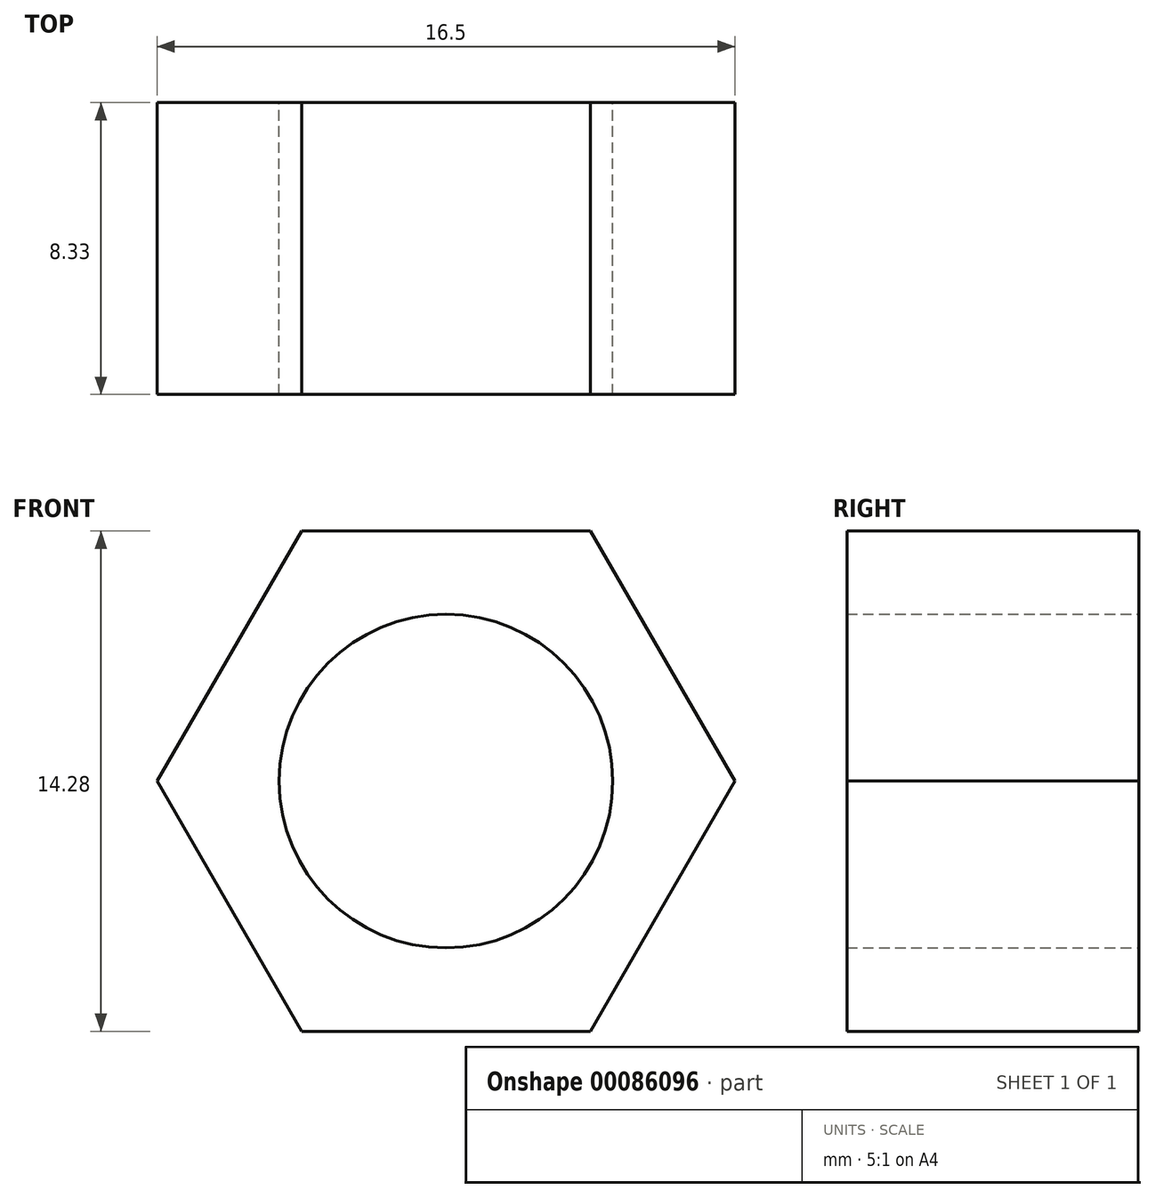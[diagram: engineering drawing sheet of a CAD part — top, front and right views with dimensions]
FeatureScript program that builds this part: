
annotation { "Feature Type Name" : "Feature", "Feature Type Description" : "" }
export const myFeature = defineFeature(function(context is Context, id is Id, definition is map)
    precondition{}
    {
        {
            var Q0;
            Q0=qCreatedBy(makeId("Front.planeOp"),FACE);
            var sketch = newSketch(context, id + "F0", { "sketchPlane" : qUnion([Q0])});
            skCircle(sketch, "E0.cCircle", {"center": v(0, 0) * mm, "radius": 7.14 * mm, "construction": true});
            skLineSegment(sketch, "E0.0", {"start": v(4.12, -7.14) * mm, "end": v(-4.12, -7.14) * mm});
            skLineSegment(sketch, "E0.1", {"start": v(-4.12, -7.14) * mm, "end": v(-8.25, 0) * mm});
            skLineSegment(sketch, "E0.2", {"start": v(-8.25, 0) * mm, "end": v(-4.12, 7.14) * mm});
            skLineSegment(sketch, "E0.3", {"start": v(-4.12, 7.14) * mm, "end": v(4.12, 7.14) * mm});
            skLineSegment(sketch, "E0.4", {"start": v(4.12, 7.14) * mm, "end": v(8.25, 0) * mm});
            skLineSegment(sketch, "E0.5", {"start": v(8.25, 0) * mm, "end": v(4.12, -7.14) * mm});
            skPoint(sketch, "E0.0.midPoint", {"position": v(0, -7.14) * mm});
            skCircle(sketch, "E1", {"center": v(0, 0) * mm, "radius": 4.76 * mm});
            skSolve(sketch);
        }
        {
            var Q0;
            Q0 = qSketchRegion(id + "F0", true);
            extrude(context, id + "F1", {"entities" : qUnion([Q0]), "depth" : 8.33 * mm});
        }
    });
